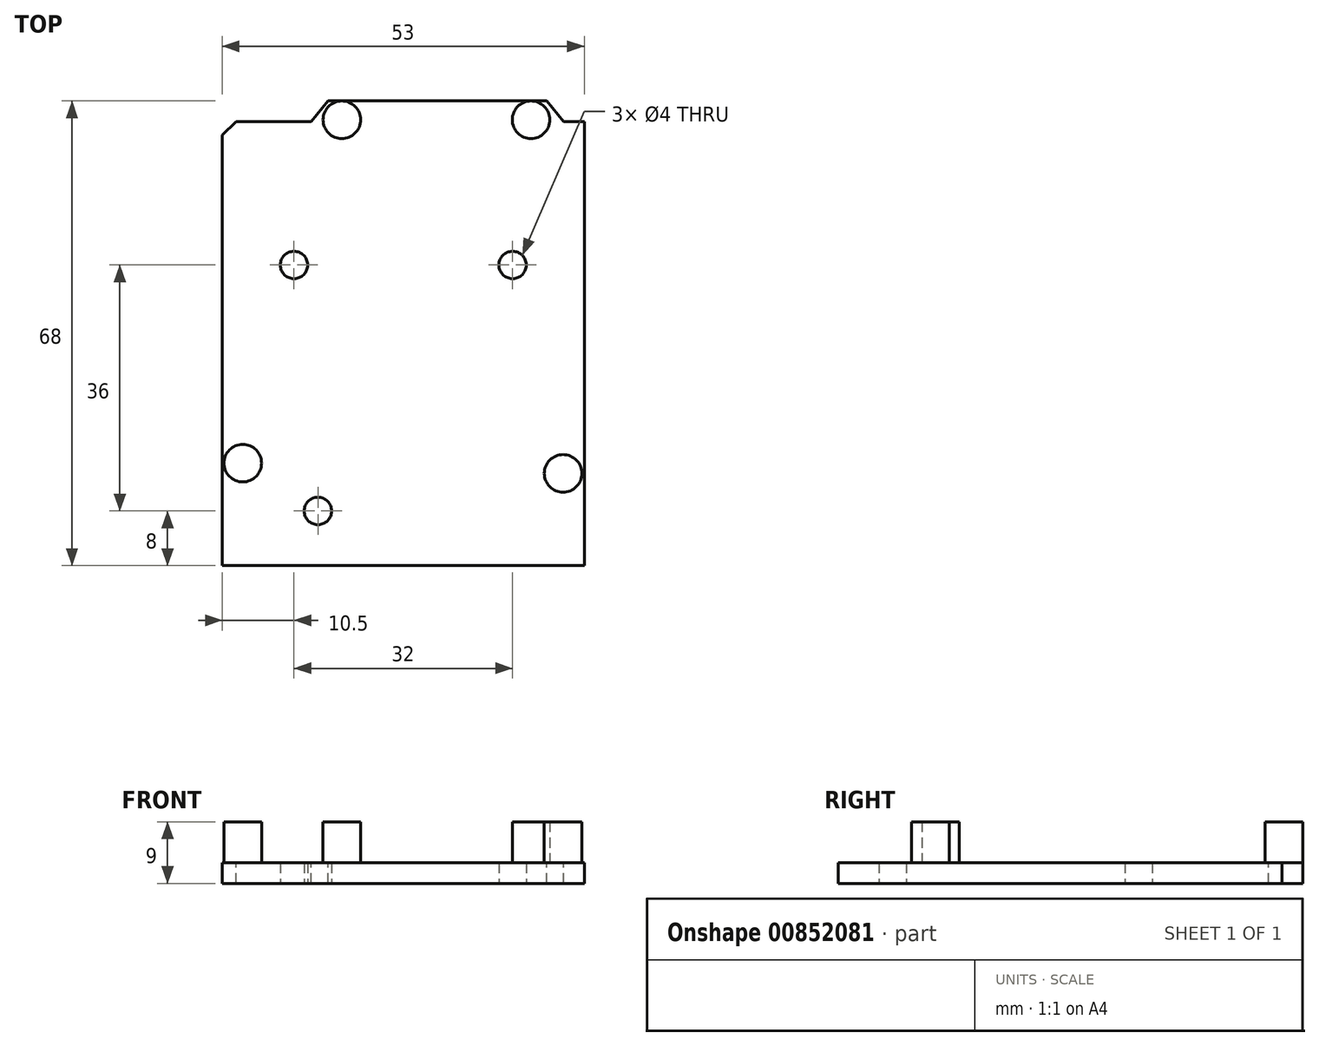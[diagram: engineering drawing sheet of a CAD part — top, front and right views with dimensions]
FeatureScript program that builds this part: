
annotation { "Feature Type Name" : "Feature", "Feature Type Description" : "" }
export const myFeature = defineFeature(function(context is Context, id is Id, definition is map)
    precondition{}
    {
        {
            var Q0;
            Q0=qCreatedBy(makeId("Top.planeOp"),FACE);
            var sketch = newSketch(context, id + "F0", { "sketchPlane" : qUnion([Q0])});
            skLineSegment(sketch, "E0.bottom", {"start": v(0, 0) * mm, "end": v(53, 0) * mm});
            skLineSegment(sketch, "E0.left", {"start": v(0, 0) * mm, "end": v(0, 63) * mm});
            skLineSegment(sketch, "E0.right", {"start": v(53, 0) * mm, "end": v(53, 65) * mm});
            skLineSegment(sketch, "E1", {"start": v(2, 65) * mm, "end": v(13, 65) * mm});
            skLineSegment(sketch, "E2", {"start": v(53, 65) * mm, "end": v(50, 65) * mm});
            skLineSegment(sketch, "E3", {"start": v(13, 65) * mm, "end": v(15.5, 68) * mm});
            skLineSegment(sketch, "E4", {"start": v(47.5, 68) * mm, "end": v(50, 65) * mm});
            skLineSegment(sketch, "E5", {"start": v(2, 65) * mm, "end": v(0, 63) * mm});
            skLineSegment(sketch, "E6.trimOffspring", {"start": v(50, 65) * mm, "end": v(53, 65) * mm});
            skLineSegment(sketch, "E7", {"start": v(15.5, 68) * mm, "end": v(47.5, 68) * mm});
            skCircle(sketch, "E8", {"center": v(45.2, 65.25) * mm, "radius": 2.75 * mm});
            skCircle(sketch, "E9", {"center": v(17.5, 65.25) * mm, "radius": 2.75 * mm});
            skCircle(sketch, "E10", {"center": v(3, 15) * mm, "radius": 2.75 * mm});
            skCircle(sketch, "E11", {"center": v(49.9, 13.5) * mm, "radius": 2.75 * mm});
            skSolve(sketch);
        }
        {
            var Q0;
            Q0 = qSketchRegion(id + "F0", true);
            var Q1;
            Q1=makeQuery(id+"F0.imprint","IMPRINT",FACE,{"disambiguationData":[TD([[makeQuery(id+"F0.imprint","IMPRINT",EDGE,{"derivedFrom":sQuery(id+"F0.wireOp",EDGE,"E10")}),1.0]])]});
            var Q2;
            Q2=makeQuery(id+"F0.imprint","IMPRINT",FACE,{"disambiguationData":[TD([[makeQuery(id+"F0.imprint","IMPRINT",EDGE,{"derivedFrom":sQuery(id+"F0.wireOp",EDGE,"E11")}),1.0]])]});
            extrude(context, id + "F1", {"entities" : qUnion([Q0, Q1, Q2]), "oppositeDirection" : true, "depth" : 3 * mm, "offsetDistance" : 25 * mm});
        }
        {
            var Q0;
            Q0=makeQuery(id+"F0.imprint","IMPRINT",FACE,{"disambiguationData":[TD([[makeQuery(id+"F0.imprint","IMPRINT",EDGE,{"derivedFrom":sQuery(id+"F0.wireOp",EDGE,"E9")}),1.0]])]});
            var Q1;
            Q1=makeQuery(id+"F0.imprint","IMPRINT",FACE,{"disambiguationData":[TD([[makeQuery(id+"F0.imprint","IMPRINT",EDGE,{"derivedFrom":sQuery(id+"F0.wireOp",EDGE,"E8")}),1.0]])]});
            var Q2;
            Q2=makeQuery(id+"F0.imprint","IMPRINT",FACE,{"disambiguationData":[TD([[makeQuery(id+"F0.imprint","IMPRINT",EDGE,{"derivedFrom":sQuery(id+"F0.wireOp",EDGE,"E11")}),1.0]])]});
            var Q3;
            Q3=makeQuery(id+"F0.imprint","IMPRINT",FACE,{"disambiguationData":[TD([[makeQuery(id+"F0.imprint","IMPRINT",EDGE,{"derivedFrom":sQuery(id+"F0.wireOp",EDGE,"E10")}),1.0]])]});
            extrude(context, id + "F2", {"entities" : qUnion([Q0, Q1, Q2, Q3]), "operationType" : NewBodyOperationType.ADD, "depth" : 6 * mm, "offsetDistance" : 25 * mm});
        }
        {
            var Q0;
            Q0=makeQuery(id+"F1.opExtrude","CAP_FACE",FACE,{"disambiguationData":[OSD([sQuery(id+"F0.wireOp",EDGE,"E0.bottom"),sQuery(id+"F0.wireOp",EDGE,"E0.left"),sQuery(id+"F0.wireOp",EDGE,"E0.right"),sQuery(id+"F0.wireOp",EDGE,"E1"),sQuery(id+"F0.wireOp",EDGE,"E3"),sQuery(id+"F0.wireOp",EDGE,"E4"),sQuery(id+"F0.wireOp",EDGE,"E5"),sQuery(id+"F0.wireOp",EDGE,"E6.trimOffspring"),sQuery(id+"F0.wireOp",EDGE,"E7")])],"isStart":false});
            var sketch = newSketch(context, id + "F3", { "sketchPlane" : qUnion([Q0])});
            skCircle(sketch, "E12", {"center": v(42.5, -44) * mm, "radius": 2 * mm});
            skCircle(sketch, "E13", {"center": v(10.5, -44) * mm, "radius": 2 * mm});
            skCircle(sketch, "E14", {"center": v(14, -8) * mm, "radius": 2 * mm});
            skSolve(sketch);
        }
        {
            var Q0;
            Q0 = qSketchRegion(id + "F3", true);
            extrude(context, id + "F4", {"entities" : qUnion([Q0]), "operationType" : NewBodyOperationType.REMOVE, "oppositeDirection" : true, "depth" : 25 * mm, "offsetDistance" : 25 * mm});
        }
    });
